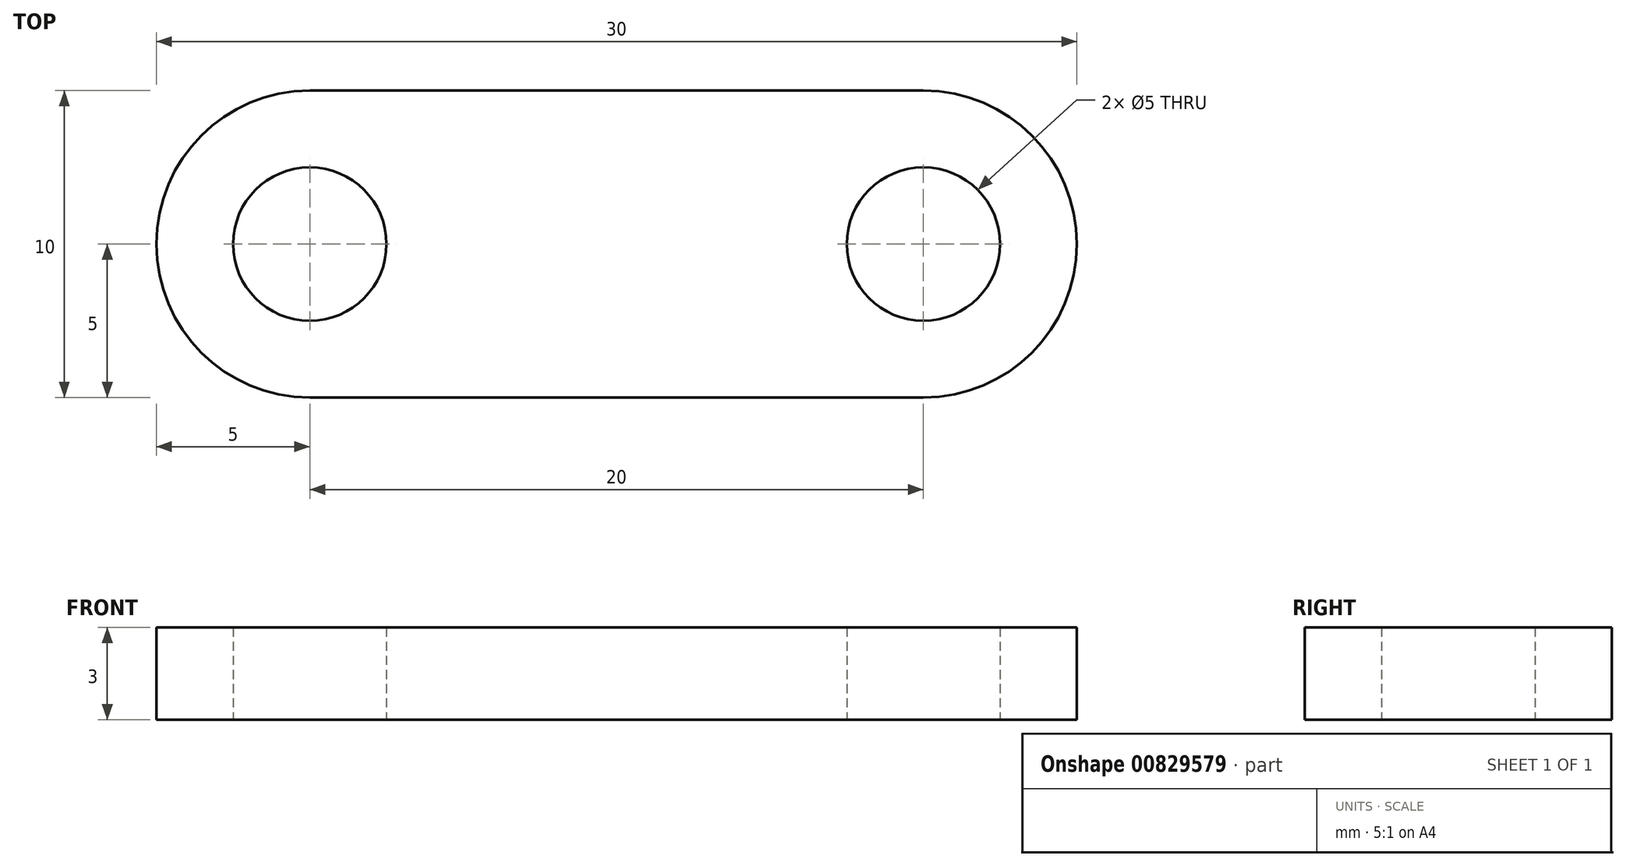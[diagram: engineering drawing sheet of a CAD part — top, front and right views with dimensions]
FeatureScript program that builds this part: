
annotation { "Feature Type Name" : "Feature", "Feature Type Description" : "" }
export const myFeature = defineFeature(function(context is Context, id is Id, definition is map)
    precondition{}
    {
        {
            var Q0;
            Q0=qCreatedBy(makeId("Top.planeOp"),FACE);
            var sketch = newSketch(context, id + "F0", { "sketchPlane" : qUnion([Q0])});
            skCircle(sketch, "E0", {"center": v(0, 0) * mm, "radius": 2.5 * mm});
            skArc(sketch, "E1", {"start": v(0, 5) * mm, "mid": v(-5, 0) * mm, "end": v(0, -5) * mm});
            skCircle(sketch, "E2", {"center": v(20, 0) * mm, "radius": 2.5 * mm});
            skArc(sketch, "E3", {"start": v(20, -5) * mm, "mid": v(25, 0) * mm, "end": v(20, 5) * mm});
            skLineSegment(sketch, "E4", {"start": v(0, 5) * mm, "end": v(20, 5) * mm});
            skLineSegment(sketch, "E5", {"start": v(0, -5) * mm, "end": v(20, -5) * mm});
            skSolve(sketch);
        }
        {
            var Q0;
            Q0 = qSketchRegion(id + "F0", true);
            extrude(context, id + "F1", {"entities" : qUnion([Q0]), "depth" : 3 * mm, "offsetDistance" : 25 * mm});
        }
    });
